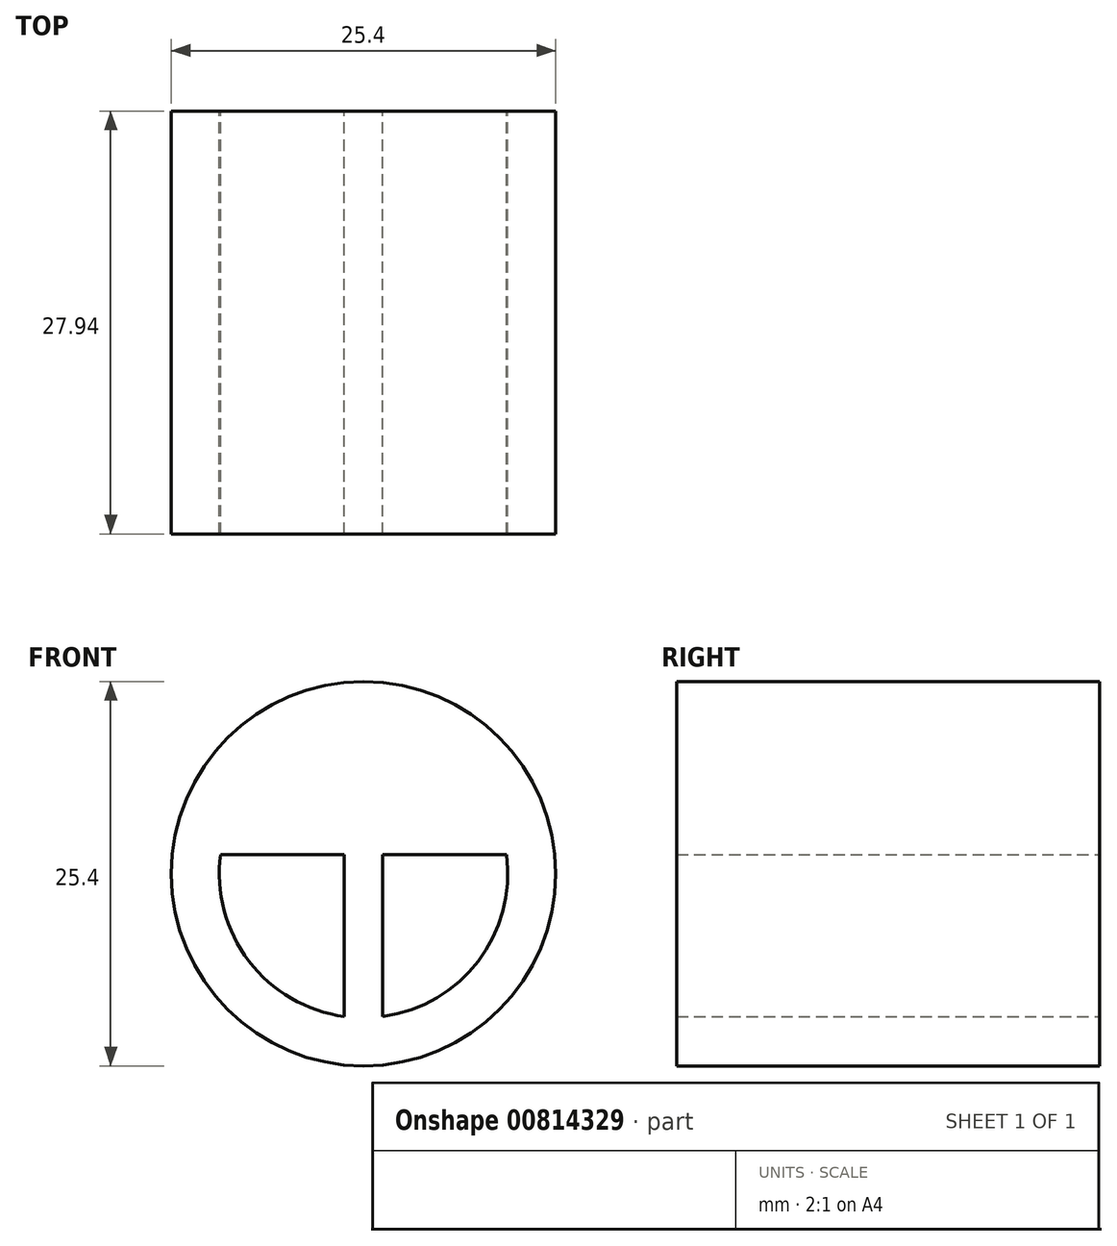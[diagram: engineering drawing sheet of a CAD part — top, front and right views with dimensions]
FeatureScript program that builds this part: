
annotation { "Feature Type Name" : "Feature", "Feature Type Description" : "" }
export const myFeature = defineFeature(function(context is Context, id is Id, definition is map)
    precondition{}
    {
        {
            var Q0;
            Q0=qCreatedBy(makeId("Front.planeOp"),FACE);
            var sketch = newSketch(context, id + "F0", { "sketchPlane" : qUnion([Q0])});
            skCircle(sketch, "E0", {"center": v(0, 0) * mm, "radius": 12.7 * mm});
            skCircle(sketch, "E1", {"center": v(0, 0) * mm, "radius": 9.53 * mm});
            skLineSegment(sketch, "E2.bottom", {"start": v(-1.27, 11.43) * mm, "end": v(1.27, 11.43) * mm});
            skLineSegment(sketch, "E2.top", {"start": v(-1.27, -11.43) * mm, "end": v(1.27, -11.43) * mm});
            skLineSegment(sketch, "E2.left", {"start": v(-1.27, 11.43) * mm, "end": v(-1.27, -11.43) * mm});
            skLineSegment(sketch, "E2.right", {"start": v(1.27, 11.43) * mm, "end": v(1.27, -11.43) * mm});
            skLineSegment(sketch, "E3.bottom", {"start": v(-11.43, 1.27) * mm, "end": v(11.43, 1.27) * mm});
            skLineSegment(sketch, "E3.top", {"start": v(-11.43, -1.27) * mm, "end": v(11.43, -1.27) * mm});
            skLineSegment(sketch, "E3.left", {"start": v(-11.43, 1.27) * mm, "end": v(-11.43, -1.27) * mm});
            skLineSegment(sketch, "E3.right", {"start": v(11.43, 1.27) * mm, "end": v(11.43, -1.27) * mm});
            skLineSegment(sketch, "E4", {"start": v(-1.27, 11.43) * mm, "end": v(1.27, -11.43) * mm, "construction": true});
            skLineSegment(sketch, "E5", {"start": v(-11.43, -1.27) * mm, "end": v(11.43, 1.27) * mm, "construction": true});
            skSolve(sketch);
        }
        {
            var Q0;
            {var subQ0=sQuery(id+"F0.wireOp",EDGE,"E3.bottom");var subQ1=sQuery(id+"F0.wireOp",EDGE,"E1");var subQ2=makeQuery(id+"F0.imprint","INTERSECT",VERTEX,{"disambiguationData":[OD(0.0)],"derivedFrom":[subQ1,subQ0]});Q0=makeQuery(id+"F0.imprint","IMPRINT",FACE,{"disambiguationData":[TD([[makeQuery(id+"F0.imprint","IMPRINT",EDGE,{"disambiguationData":[TD([[subQ2,1.0]])],"derivedFrom":subQ1}),1.0]])]});}
            var Q1;
            {var subQ0=sQuery(id+"F0.wireOp",EDGE,"E3.bottom");var subQ1=sQuery(id+"F0.wireOp",EDGE,"E1");var subQ2=makeQuery(id+"F0.imprint","INTERSECT",VERTEX,{"disambiguationData":[OD(1.0)],"derivedFrom":[subQ1,subQ0]});Q1=makeQuery(id+"F0.imprint","IMPRINT",FACE,{"disambiguationData":[TD([[makeQuery(id+"F0.imprint","IMPRINT",EDGE,{"disambiguationData":[TD([[subQ2,-1.0]])],"derivedFrom":subQ1}),1.0]])]});}
            var Q2;
            {var subQ5=sQuery(id+"F0.wireOp",EDGE,"E3.left");Q2=makeQuery(id+"F0.imprint","IMPRINT",FACE,{"disambiguationData":[TD([[makeQuery(id+"F0.imprint","IMPRINT",EDGE,{"derivedFrom":subQ5}),1.0]])]});}
            var Q3;
            {var subQ0=sQuery(id+"F0.wireOp",EDGE,"E2.right");var subQ1=sQuery(id+"F0.wireOp",EDGE,"E1");var subQ2=makeQuery(id+"F0.imprint","INTERSECT",VERTEX,{"disambiguationData":[OD(0.0)],"derivedFrom":[subQ1,subQ0]});Q3=makeQuery(id+"F0.imprint","IMPRINT",FACE,{"disambiguationData":[TD([[makeQuery(id+"F0.imprint","IMPRINT",EDGE,{"disambiguationData":[TD([[subQ2,-1.0]])],"derivedFrom":subQ1}),1.0]])]});}
            var Q4;
            Q4=makeQuery(id+"F0.imprint","IMPRINT",FACE,{"disambiguationData":[TD([[makeQuery(id+"F0.imprint","IMPRINT",EDGE,{"derivedFrom":sQuery(id+"F0.wireOp",EDGE,"E0")}),1.0]])]});
            var Q5;
            {var subQ5=sQuery(id+"F0.wireOp",EDGE,"E2.bottom");Q5=makeQuery(id+"F0.imprint","IMPRINT",FACE,{"disambiguationData":[TD([[makeQuery(id+"F0.imprint","IMPRINT",EDGE,{"derivedFrom":subQ5}),-1.0]])]});}
            var Q6;
            {var subQ0=sQuery(id+"F0.wireOp",EDGE,"E2.left");var subQ1=sQuery(id+"F0.wireOp",EDGE,"E1");var subQ2=makeQuery(id+"F0.imprint","INTERSECT",VERTEX,{"disambiguationData":[OD(1.0)],"derivedFrom":[subQ1,subQ0]});Q6=makeQuery(id+"F0.imprint","IMPRINT",FACE,{"disambiguationData":[TD([[makeQuery(id+"F0.imprint","IMPRINT",EDGE,{"disambiguationData":[TD([[subQ2,-1.0]])],"derivedFrom":subQ1}),1.0]])]});}
            var Q7;
            {var subQ5=sQuery(id+"F0.wireOp",EDGE,"E2.top");Q7=makeQuery(id+"F0.imprint","IMPRINT",FACE,{"disambiguationData":[TD([[makeQuery(id+"F0.imprint","IMPRINT",EDGE,{"derivedFrom":subQ5}),1.0]])]});}
            var Q8;
            {var subQ5=sQuery(id+"F0.wireOp",EDGE,"E3.right");Q8=makeQuery(id+"F0.imprint","IMPRINT",FACE,{"disambiguationData":[TD([[makeQuery(id+"F0.imprint","IMPRINT",EDGE,{"derivedFrom":subQ5}),-1.0]])]});}
            var Q9;
            {var subQ0=sQuery(id+"F0.wireOp",EDGE,"E3.bottom");var subQ1=sQuery(id+"F0.wireOp",EDGE,"E2.left");var subQ2=makeQuery(id+"F0.imprint","INTERSECT",VERTEX,{"derivedFrom":[subQ1,subQ0]});Q9=makeQuery(id+"F0.imprint","IMPRINT",FACE,{"disambiguationData":[TD([[makeQuery(id+"F0.imprint","IMPRINT",EDGE,{"disambiguationData":[TD([[subQ2,-1.0]])],"derivedFrom":subQ1}),1.0]])]});}
            extrude(context, id + "F1", {"entities" : qUnion([Q0, Q1, Q2, Q3, Q4, Q5, Q6, Q7, Q8, Q9]), "depth" : 27.94 * mm, "offsetDistance" : 25.4 * mm});
        }
    });
